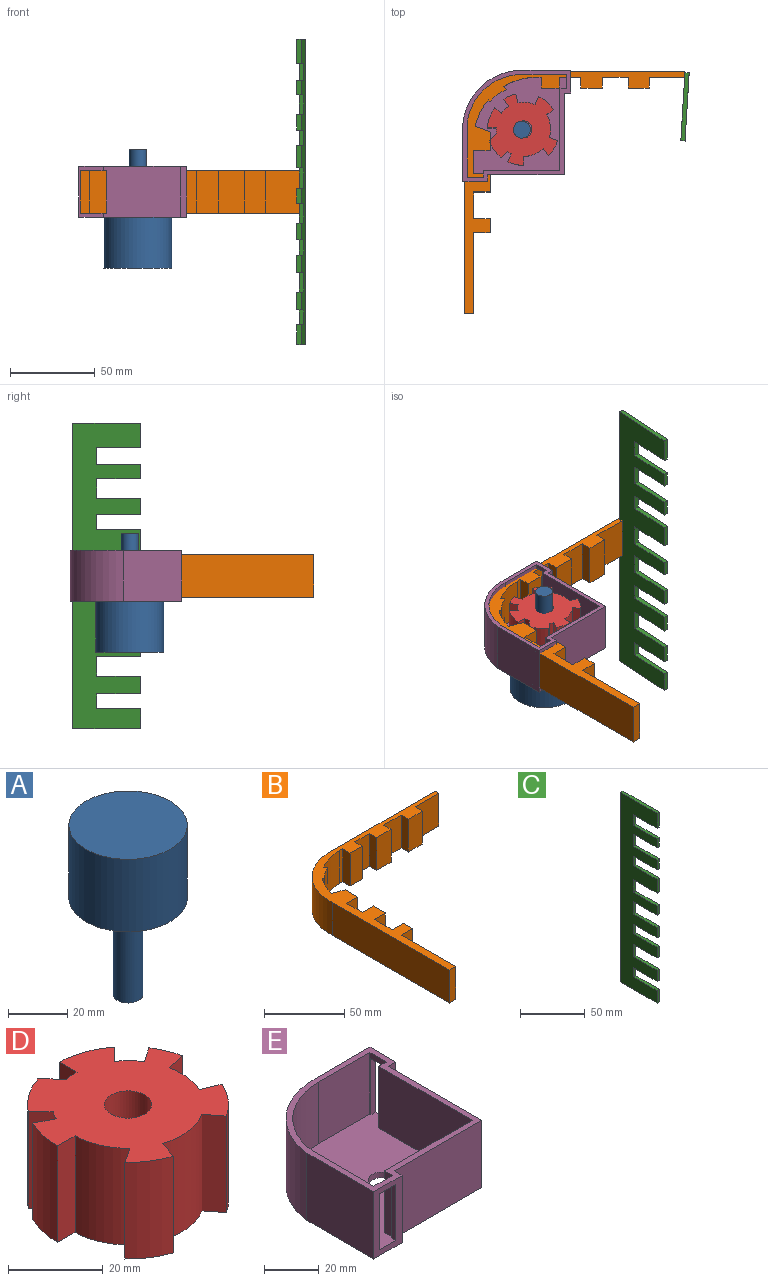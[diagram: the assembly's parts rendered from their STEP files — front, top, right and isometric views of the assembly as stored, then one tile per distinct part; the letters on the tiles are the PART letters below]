
ASSEMBLY  parts=5 mates=4
PART A: 5 faces, bbox 40x40x70 mm
  f0: cylinder r=5mm len=40mm, axis (0,0,-1), area 1256.6mm2, adj f1,f4
  f1: plane 10x10mm, normal (0,0,-1), area 78.5mm2, adj f0
  f2: cylinder r=20mm len=40mm, axis (0,0,-1), area 3769.9mm2, adj f3,f4
  f3: plane 40x40mm, normal (0,0,1), area 1256.6mm2, adj f2
  f4: plane 40x40mm, normal (0,0,-1), area 1178.1mm2, adj f0,f2
PART B: 39 faces, bbox 130.4x142.6x25 mm
  f0: plane 25x13.56mm, normal (1,0,0), area 339.1mm2, adj f1,f36,f37,f38
  f1: plane 25x9.74mm, normal (0,-1,0), area 243.5mm2, adj f0,f2,f37,f38
  f2: plane 25x11.06mm, normal (1,0,0), area 276.6mm2, adj f1,f3,f37,f38
  f3: plane 25x8.89mm, normal (0.35,0.94,0), area 237.7mm2, adj f2,f4,f37,f38
  f4: cylinder r=37.2mm len=25mm, axis (0,0,-1), area 436.8mm2, adj f3,f5,f37,f38
  f5: plane 25x1.03mm, normal (-0.72,-0.7,0), area 35.8mm2, adj f4,f6,f37,f38
  f6: cylinder r=24.79mm len=25mm, axis (0,0,-1), area 6.7mm2, adj f5,f7,f37,f38
  f7: plane 25x0.09mm, normal (0.76,-0.66,0), area 3mm2, adj f6,f8,f37,f38
  f8: cylinder r=24.79mm len=25mm, axis (0,0,-1), area 296.5mm2, adj f7,f9,f37,f38
  f9: plane 25x1.84mm, normal (0.72,0.7,0), area 64.2mm2, adj f8,f10,f37,f38
  f10: cylinder r=37.2mm len=25mm, axis (0,0,-1), area 514.9mm2, adj f9,f11,f37,f38
  f11: plane 25x2.74mm, normal (0,-1,0), area 68.4mm2, adj f10,f12,f37,f38
  f12: plane 25x6.43mm, normal (-1,0,0), area 160.7mm2, adj f11,f13,f37,f38
  f13: plane 25x10.61mm, normal (0,-1,0), area 265.3mm2, adj f12,f14,f37,f38
  f14: plane 25x6.43mm, normal (1,0,0), area 160.7mm2, adj f13,f15,f37,f38
  f15: plane 25x12.73mm, normal (0,-1,0), area 318.3mm2, adj f14,f16,f37,f38
  f16: plane 25x6.43mm, normal (-1,0,0), area 160.7mm2, adj f15,f17,f37,f38
  f17: plane 25x12.73mm, normal (0,-1,0), area 318.3mm2, adj f16,f18,f37,f38
  f18: plane 25x6.43mm, normal (1,0,0), area 160.7mm2, adj f17,f19,f37,f38
  f19: plane 25x15.28mm, normal (0,-1,0), area 382mm2, adj f18,f20,f37,f38
  f20: plane 25x6.43mm, normal (-1,0,0), area 160.7mm2, adj f19,f21,f37,f38
  f21: plane 25x12.31mm, normal (0,-1,0), area 307.7mm2, adj f20,f22,f37,f38
  f22: plane 25x6.43mm, normal (1,0,0), area 160.7mm2, adj f21,f23,f37,f38
  f23: plane 25x20.92mm, normal (0,-1,0), area 522.9mm2, adj f22,f24,f37,f38
  f24: plane 25x3.22mm, normal (1,-0.06,0), area 80.5mm2, adj f23,f25,f37,f38
  f25: plane 93.16x25mm, normal (0,1,0), area 2328.9mm2, adj f24,f26,f37,f38
  f26: cylinder r=37.2mm len=39.62mm, axis (0,0,-1), area 1521.3mm2, adj f25,f27,f37,f38
  f27: plane 103x25mm, normal (-1,0,0), area 2575.1mm2, adj f26,f28,f37,f38
  f28: plane 25x5.64mm, normal (0,-1,0), area 141.1mm2, adj f27,f29,f37,f38
  f29: plane 47.83x25mm, normal (1,0,0), area 1195.7mm2, adj f28,f30,f37,f38
  f30: plane 25x9.74mm, normal (0,-1,0), area 243.5mm2, adj f29,f31,f37,f38
  f31: plane 25x8.21mm, normal (1,0,0), area 205.2mm2, adj f30,f32,f37,f38
  f32: plane 25x9.74mm, normal (0,1,0), area 243.5mm2, adj f31,f33,f37,f38
  f33: plane 25x15.7mm, normal (1,0,0), area 392.6mm2, adj f32,f34,f37,f38
  f34: plane 25x9.74mm, normal (0,-1,0), area 243.5mm2, adj f33,f35,f37,f38
  f35: plane 25x10.71mm, normal (1,0,0), area 267.7mm2, adj f34,f36,f37,f38
  f36: plane 25x9.74mm, normal (0,1,0), area 243.5mm2, adj f0,f35,f37,f38
  f37: plane 142.62x130.35mm, normal (0,0,1), area 1764.1mm2, adj f0,f1,f2,f3,f4,f5,f6,f7
  f38: plane 142.62x130.35mm, normal (0,0,-1), area 1764.1mm2, adj f0,f1,f2,f3,f4,f5,f6,f7
PART C: 38 faces, bbox 2.5x40x180 mm
  f0: plane 180x2.5mm, normal (0,1,0), area 450mm2, adj f1,f35,f36,f37
  f1: plane 40x2.5mm, normal (0,0,1), area 100mm2, adj f0,f2,f36,f37
  f2: plane 14.22x2.5mm, normal (0,-1,0), area 35.6mm2, adj f1,f3,f36,f37
  f3: plane 25.91x2.5mm, normal (0,0,-1), area 64.8mm2, adj f2,f4,f36,f37
  f4: plane 10.04x2.5mm, normal (0,-1,0), area 25.1mm2, adj f3,f5,f36,f37
  f5: plane 25.91x2.5mm, normal (0,0,1), area 64.8mm2, adj f4,f6,f36,f37
  f6: plane 8.29x2.5mm, normal (0,-1,0), area 20.7mm2, adj f5,f7,f36,f37
  f7: plane 25.91x2.5mm, normal (0,0,-1), area 64.8mm2, adj f6,f8,f36,f37
  f8: plane 11.78x2.5mm, normal (0,-1,0), area 29.5mm2, adj f7,f9,f36,f37
  f9: plane 25.91x2.5mm, normal (0,0,1), area 64.8mm2, adj f8,f10,f36,f37
  f10: plane 9.16x2.5mm, normal (0,-1,0), area 22.9mm2, adj f9,f11,f36,f37
  f11: plane 25.91x2.5mm, normal (0,0,-1), area 64.8mm2, adj f10,f12,f36,f37
  f12: plane 9.16x2.5mm, normal (0,-1,0), area 22.9mm2, adj f11,f13,f36,f37
  f13: plane 25.91x2.5mm, normal (0,0,1), area 64.8mm2, adj f12,f14,f36,f37
  f14: plane 13.09x2.5mm, normal (0,-1,0), area 32.7mm2, adj f13,f15,f36,f37
  f15: plane 25.91x2.5mm, normal (0,0,-1), area 64.8mm2, adj f14,f16,f36,f37
  f16: plane 12.22x2.5mm, normal (0,-1,0), area 30.5mm2, adj f15,f17,f36,f37
  f17: plane 25.91x2.5mm, normal (0,0,1), area 64.8mm2, adj f16,f18,f36,f37
  f18: plane 8.73x2.5mm, normal (0,-1,0), area 21.8mm2, adj f17,f19,f36,f37
  f19: plane 25.91x2.5mm, normal (0,0,-1), area 64.8mm2, adj f18,f20,f36,f37
  f20: plane 11.78x2.5mm, normal (0,-1,0), area 29.5mm2, adj f19,f21,f36,f37
  f21: plane 25.91x2.5mm, normal (0,0,1), area 64.8mm2, adj f20,f22,f36,f37
  f22: plane 9.6x2.5mm, normal (0,-1,0), area 24mm2, adj f21,f23,f36,f37
  f23: plane 25.91x2.5mm, normal (0,0,-1), area 64.8mm2, adj f22,f24,f36,f37
  f24: plane 9.16x2.5mm, normal (0,-1,0), area 22.9mm2, adj f23,f25,f36,f37
  f25: plane 25.91x2.5mm, normal (0,0,1), area 64.8mm2, adj f24,f26,f36,f37
  f26: plane 10.04x2.5mm, normal (0,-1,0), area 25.1mm2, adj f25,f27,f36,f37
  f27: plane 25.91x2.5mm, normal (0,0,-1), area 64.8mm2, adj f26,f28,f36,f37
  f28: plane 11.78x2.5mm, normal (0,-1,0), area 29.5mm2, adj f27,f29,f36,f37
  f29: plane 25.91x2.5mm, normal (0,0,1), area 64.8mm2, adj f28,f30,f36,f37
  f30: plane 10.47x2.5mm, normal (0,-1,0), area 26.2mm2, adj f29,f31,f36,f37
  f31: plane 25.91x2.5mm, normal (0,0,-1), area 64.8mm2, adj f30,f32,f36,f37
  f32: plane 8.73x2.5mm, normal (0,-1,0), area 21.8mm2, adj f31,f33,f36,f37
  f33: plane 25.91x2.5mm, normal (0,0,1), area 64.8mm2, adj f32,f34,f36,f37
  f34: plane 11.75x2.5mm, normal (0,-1,0), area 29.4mm2, adj f33,f35,f36,f37
  f35: plane 40x2.5mm, normal (0,0,-1), area 100mm2, adj f0,f34,f36,f37
  f36: plane 180x40mm, normal (1,0,0), area 5006.5mm2, adj f0,f1,f2,f3,f4,f5,f6,f7
  f37: plane 180x40mm, normal (-1,0,0), area 5006.5mm2, adj f0,f1,f2,f3,f4,f5,f6,f7
PART D: 29 faces, bbox 42x41.4x25 mm
  f0: plane 25x4.88mm, normal (0.94,-0.35,0), area 130mm2, adj f1,f25,f27,f28
  f1: cylinder r=16.06mm len=25mm, axis (0,0,-1), area 348.1mm2, adj f0,f2,f27,f28
  f2: plane 25x4.13mm, normal (-0.79,-0.61,0), area 130.3mm2, adj f1,f3,f27,f28
  f3: cylinder r=21.25mm len=25mm, axis (0,0,-1), area 297.9mm2, adj f2,f4,f27,f28
  f4: plane 25x4.81mm, normal (0.38,0.93,0), area 130mm2, adj f3,f5,f27,f28
  f5: cylinder r=16.06mm len=25mm, axis (0,0,-1), area 262.4mm2, adj f4,f6,f27,f28
  f6: plane 25x5.08mm, normal (0.21,-0.98,0), area 129.9mm2, adj f5,f7,f27,f28
  f7: cylinder r=21.25mm len=25mm, axis (0,0,-1), area 192.5mm2, adj f6,f8,f27,f28
  f8: plane 25x4.28mm, normal (-0.57,0.82,0), area 129.9mm2, adj f7,f9,f27,f28
  f9: cylinder r=16.06mm len=25mm, axis (0,0,-1), area 158.8mm2, adj f8,f10,f27,f28
  f10: plane 25x3.78mm, normal (0.7,-0.72,0), area 131.7mm2, adj f9,f11,f27,f28
  f11: cylinder r=21.25mm len=25mm, axis (0,0,-1), area 328.2mm2, adj f10,f12,f27,f28
  f12: plane 25x5.2mm, normal (-1,0,0), area 130mm2, adj f11,f13,f27,f28
  f13: cylinder r=16.06mm len=25mm, axis (0,0,-1), area 86.7mm2, adj f12,f14,f27,f28
  f14: plane 25x4.29mm, normal (0.72,0.7,0), area 149.4mm2, adj f13,f15,f27,f28
  f15: cylinder r=21.25mm len=25mm, axis (0,0,-1), area 297.8mm2, adj f14,f16,f27,f28
  f16: plane 25x0.09mm, normal (-0.78,0.63,0), area 3mm2, adj f15,f17,f27,f28
  f17: cylinder r=21.25mm len=25mm, axis (0,0,-1), area 6.8mm2, adj f16,f18,f27,f28
  f18: plane 25x3.77mm, normal (-0.72,-0.7,0), area 131.5mm2, adj f17,f19,f27,f28
  f19: cylinder r=16.06mm len=25mm, axis (0,0,-1), area 66.1mm2, adj f18,f20,f27,f28
  f20: plane 25x4.63mm, normal (0.45,0.89,0), area 129.9mm2, adj f19,f21,f27,f28
  f21: cylinder r=21.25mm len=25mm, axis (0,0,-1), area 249.1mm2, adj f20,f22,f27,f28
  f22: plane 25x5.19mm, normal (0,-1,0), area 129.9mm2, adj f21,f23,f27,f28
  f23: cylinder r=16.06mm len=25mm, axis (0,0,-1), area 320.1mm2, adj f22,f24,f27,f28
  f24: plane 25x4.42mm, normal (-0.55,0.84,0), area 132.4mm2, adj f23,f25,f27,f28
  f25: cylinder r=21.25mm len=25mm, axis (0,0,-1), area 264.3mm2, adj f0,f24,f27,f28
  f26: cylinder r=5mm len=25mm, axis (0,0,-1), area 785.4mm2, adj f27,f28
  f27: plane 42.01x41.41mm, normal (0,0,1), area 1034.5mm2, adj f0,f1,f2,f3,f4,f5,f6,f7
  f28: plane 42.01x41.41mm, normal (0,0,-1), area 1034.5mm2, adj f0,f1,f2,f3,f4,f5,f6,f7
PART E: 28 faces, bbox 63.6x65.6x30 mm
  f0: plane 30x14.58mm, normal (0,-1,0), area 231mm2, adj f2,f7,f8,f11,f20,f25,f26,f27
  f1: plane 27.5x8.39mm, normal (-1,0,0), area 43.2mm2, adj f2,f12,f13,f20,f22,f23,f24
  f2: plane 65.61x63.63mm, normal (0,0,1), area 585.5mm2, adj f0,f1,f3,f4,f5,f6,f7,f8
  f3: plane 30x3.84mm, normal (0,-1,0), area 115.2mm2, adj f2,f4,f10,f11
  f4: plane 30x13.39mm, normal (1,0,0), area 214.2mm2, adj f2,f3,f5,f11,f20,f22,f23,f24
  f5: plane 30x28.84mm, normal (0,1,0), area 865.3mm2, adj f2,f4,f6,f11
  f6: cylinder r=35mm len=34.79mm, axis (0,0,-1), area 1533.4mm2, adj f2,f5,f7,f11
  f7: plane 34.46x30mm, normal (-1,0,0), area 1033.8mm2, adj f0,f2,f6,f11
  f8: plane 30x4.04mm, normal (1,0,0), area 121.2mm2, adj f0,f2,f9,f11
  f9: plane 45.21x30mm, normal (0,-1,0), area 1356.3mm2, adj f2,f8,f10,f11
  f10: plane 48.17x30mm, normal (1,0,0), area 1445.2mm2, adj f2,f3,f9,f11
  f11: plane 65.61x63.63mm, normal (0,0,-1), area 3456.8mm2, adj f0,f3,f4,f5,f6,f7,f8,f9
  f12: plane 27.5x3.84mm, normal (0,1,0), area 105.6mm2, adj f1,f2,f19,f20
  f13: plane 27.5x26.34mm, normal (0,-1,0), area 724.5mm2, adj f1,f2,f14,f20
  f14: cylinder r=32.5mm len=32.29mm, axis (0,0,-1), area 1301.5mm2, adj f2,f13,f15,f20
  f15: plane 31.82x27.5mm, normal (1,0,0), area 875.1mm2, adj f2,f14,f16,f20
  f16: plane 27.5x9.58mm, normal (0,1,0), area 57mm2, adj f2,f15,f17,f20,f25,f26,f27
  f17: plane 27.5x4.04mm, normal (-1,0,0), area 111.1mm2, adj f2,f16,f18,f20
  f18: plane 45.21x27.5mm, normal (0,1,0), area 1243.3mm2, adj f2,f17,f19,f20
  f19: plane 48.17x27.5mm, normal (-1,0,0), area 1324.8mm2, adj f2,f12,f18,f20
  f20: plane 63.11x61.13mm, normal (0,0,1), area 2910.7mm2, adj f0,f1,f4,f12,f13,f14,f15,f16
  f21: cylinder r=5mm len=10mm, axis (0,0,1), area 78.5mm2, adj f11,f20
  f22: plane 7.5x2.5mm, normal (0,0,-1), area 18.8mm2, adj f1,f4,f23,f24
  f23: plane 25x2.5mm, normal (0,-1,0), area 62.5mm2, adj f1,f4,f20,f22
  f24: plane 25x2.5mm, normal (0,1,0), area 62.5mm2, adj f1,f4,f20,f22
  f25: plane 8.26x2.5mm, normal (0,0,-1), area 20.6mm2, adj f0,f16,f26,f27
  f26: plane 25x2.5mm, normal (1,0,0), area 62.5mm2, adj f0,f16,f20,f25
  f27: plane 25x2.5mm, normal (-1,0,0), area 62.5mm2, adj f0,f16,f20,f25
PLACE A rot(axis=(1,0,0),180deg) t=(-174.73,152.23,1.14)mm
PLACE B t=(-21,43.41,-36.36)mm
PLACE C rot(axis=(0,0,-1),3.5deg) t=(260.93,-4.89,-271.67)mm
PLACE D rot(axis=(0,0,1),90deg) t=(184.14,-135.98,-36.36)mm
PLACE E t=(-218.34,42.93,-38.86)mm
MATE fastened C.f37 <-> B.f24  axis (-1,0.06,0) through (265.44,69.84,-23.86)mm
MATE revolute E.f6 <-> D.f28  axis (0,0,1) through (170.29,53.15,-36.36)mm
MATE revolute E.f6 <-> A.f0  axis (0,0,-1) through (170.29,53.15,-38.86)mm
MATE fastened E.f20 <-> B.f38  axis (0,0,1) through (166.86,55.66,-36.36)mm
